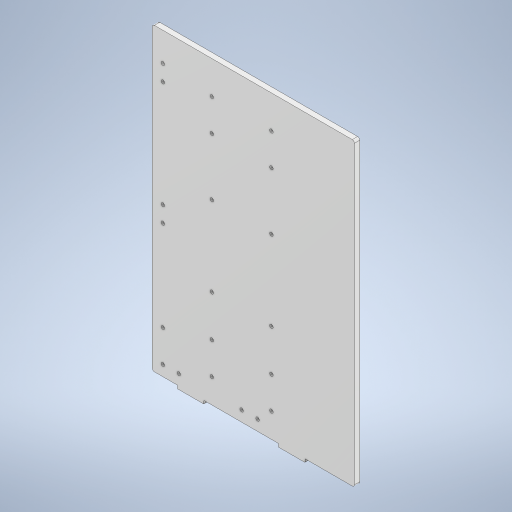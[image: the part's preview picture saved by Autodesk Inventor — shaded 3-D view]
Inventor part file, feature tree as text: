
AUTODESK INVENTOR PART (.ipt)
format: ipt  version: 2024.3 (Build 283343000, 343)  size: 930,304 bytes
history: native  units: mm
features: sketch x13, extrude x10, projected_geometry x6, fillet x4, hole x3, other x1, mirror x1
ambient origin geometry x8: Origin, YZ Plane, XZ Plane, XY Plane, X Axis, Y Axis, Z Axis, Center Point
bodies: Body1 (feature_tree)
feature tree (38):
  other  "ソリッド2"
  extrude  "押し出し20"  Depth=190.0mm
  hole  "穴2"  [1 undecoded]
  hole  "穴3"  [1 undecoded]
  extrude  "押し出し21"  Depth=56.0mm
  extrude  "押し出し22"  Depth=30.0mm
  fillet  "フィレット2"  Radius=30.0mm
  extrude  "押し出し23"  Depth=56.0mm
  extrude  "押し出し24"  Depth=56.0mm
  extrude  "押し出し25"  Depth=56.0mm
  fillet  "フィレット3"  Radius=30.0mm
  fillet  "フィレット4"  Radius=30.0mm
  hole  "穴4"  [1 undecoded]
  extrude  "押し出し26"  Depth=75.0mm
  extrude  "押し出し27"  Depth=56.0mm
  extrude  "押し出し28"  Depth=56.0mm
  fillet  "フィレット5"  Radius=26.0mm
  mirror  "ミラー1"
  extrude  "押し出し29"  Depth=26.0mm
  sketch  "スケッチ22"
  sketch  "スケッチ23"
  sketch  "スケッチ24"
  sketch  "スケッチ25"
  sketch  "スケッチ26"
  sketch  "スケッチ27"
  sketch  "スケッチ28"
  projected_geometry  "投影ループ2"
  sketch  "スケッチ29"
  projected_geometry  "投影ループ3"
  sketch  "スケッチ31"
  sketch  "スケッチ32"
  projected_geometry  "投影ループ4"
  projected_geometry  "投影ループ5"
  projected_geometry  "投影ループ6"
  sketch  "スケッチ34"
  sketch  "スケッチ36"
  projected_geometry  "投影ループ8"
  sketch  "スケッチ37"
note: 3 required parameter values undecoded (feature->parameter linkage not recoverable at this tier; creation-order binding heuristic only, values carry confidence <= 0.55)
